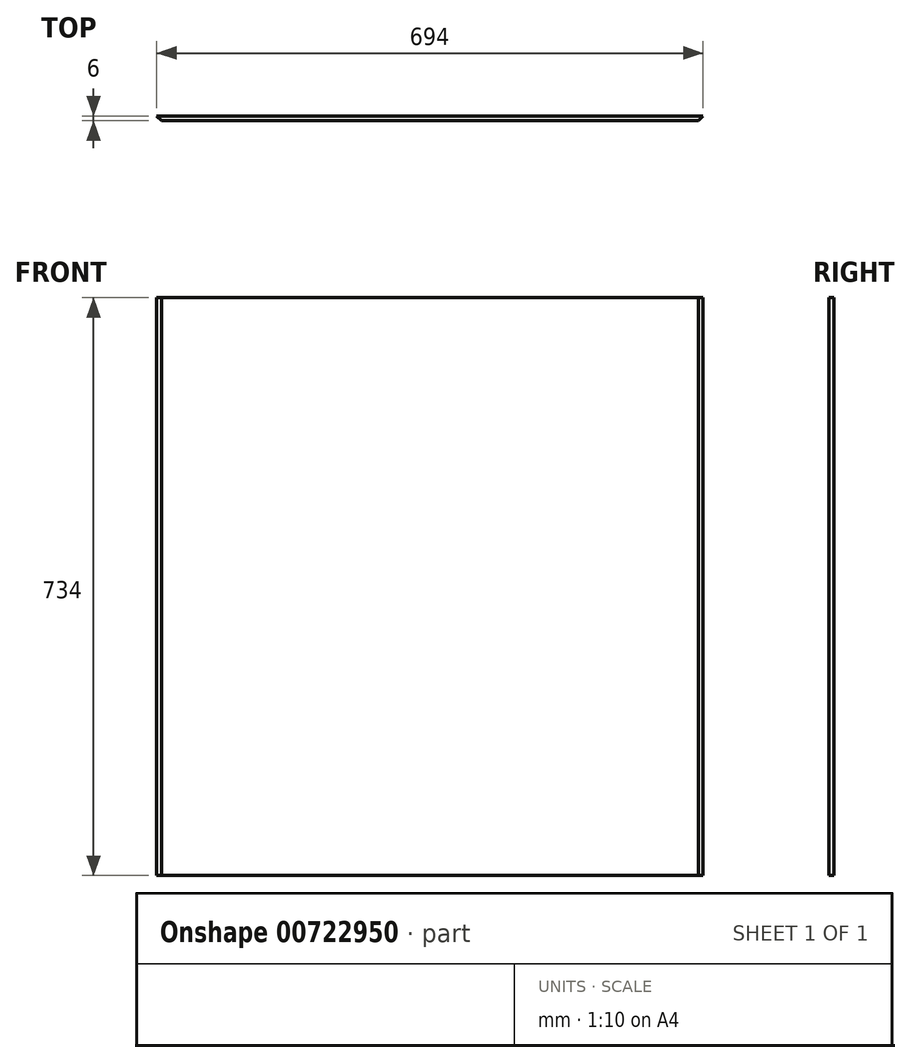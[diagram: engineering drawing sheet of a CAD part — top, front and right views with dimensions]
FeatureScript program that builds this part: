
annotation { "Feature Type Name" : "Feature", "Feature Type Description" : "" }
export const myFeature = defineFeature(function(context is Context, id is Id, definition is map)
    precondition{}
    {
        {
            var Q0;
            Q0=qCreatedBy(makeId("Front.planeOp"),FACE);
            var sketch = newSketch(context, id + "F0", { "sketchPlane" : qUnion([Q0])});
            skLineSegment(sketch, "E0.bottom", {"start": v(-347, 367) * mm, "end": v(347, 367) * mm});
            skLineSegment(sketch, "E0.top", {"start": v(-347, -367) * mm, "end": v(347, -367) * mm});
            skLineSegment(sketch, "E0.left", {"start": v(-347, 367) * mm, "end": v(-347, -367) * mm});
            skLineSegment(sketch, "E0.right", {"start": v(347, 367) * mm, "end": v(347, -367) * mm});
            skLineSegment(sketch, "E1", {"start": v(-347, 367) * mm, "end": v(347, -367) * mm, "construction": true});
            skSolve(sketch);
        }
        {
            var Q0;
            Q0 = qSketchRegion(id + "F0", true);
            extrude(context, id + "F1", {"entities" : qUnion([Q0]), "depth" : 6 * mm, "offsetDistance" : 25 * mm});
        }
        {
            var Q0;
            Q0=makeQuery(id+"F1.opExtrude","CAP_EDGE",EDGE,{"disambiguationData":[OSD([sQuery(id+"F0.wireOp",EDGE,"E0.left")])],"isStart":false});
            var Q1;
            Q1=makeQuery(id+"F1.opExtrude","CAP_EDGE",EDGE,{"disambiguationData":[OSD([sQuery(id+"F0.wireOp",EDGE,"E0.right")])],"isStart":false});
            chamfer(context, id + "F2", {"entities" : qUnion([Q0, Q1]), "width" : 6 * mm, "tangentPropagation" : true});
        }
    });
